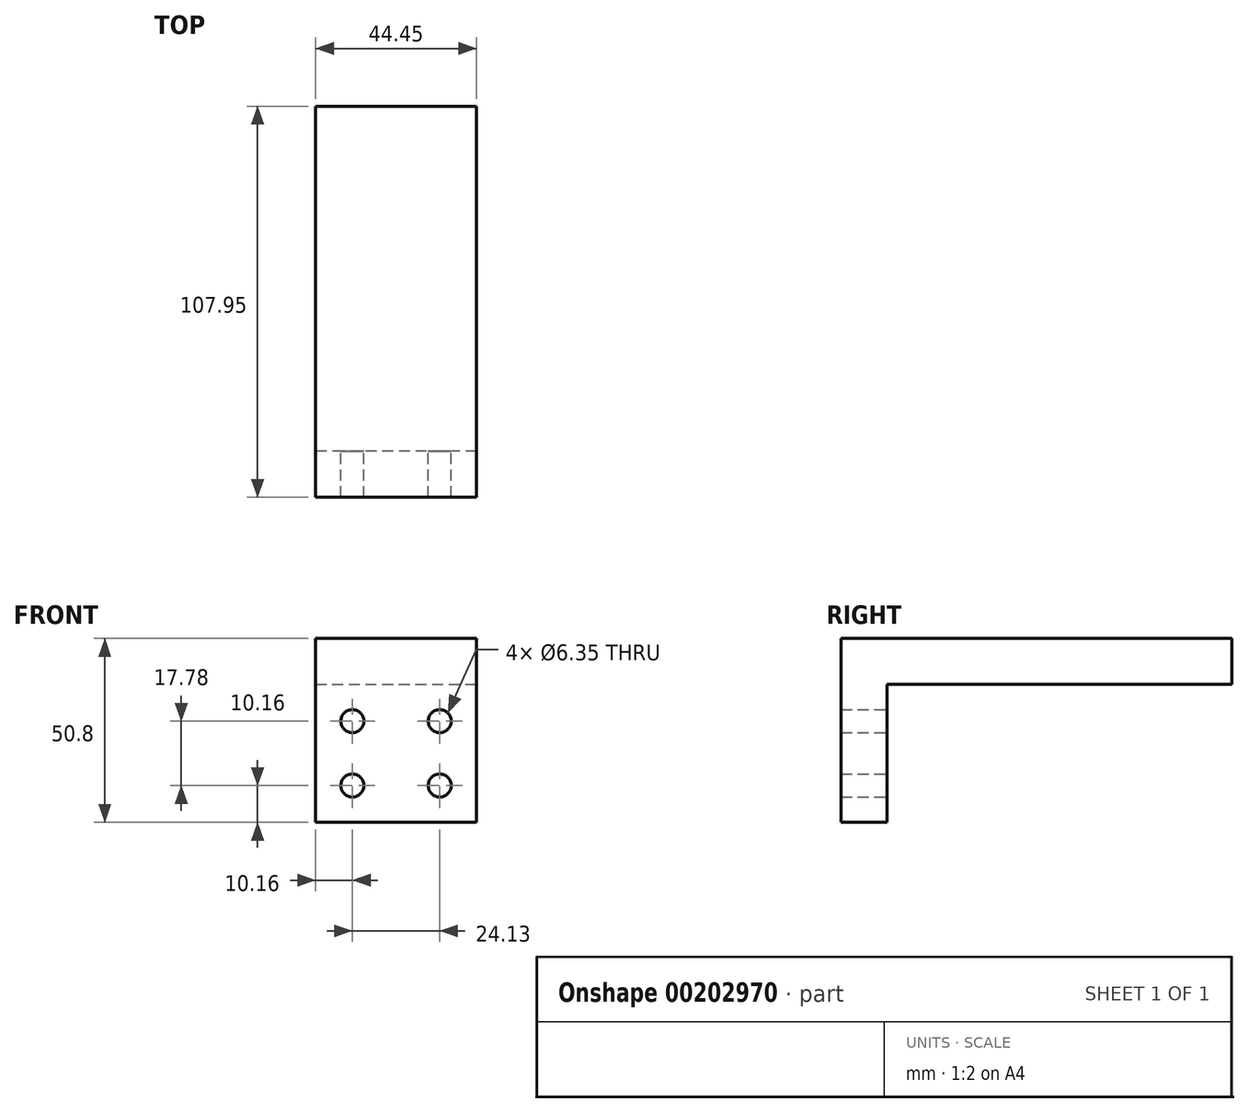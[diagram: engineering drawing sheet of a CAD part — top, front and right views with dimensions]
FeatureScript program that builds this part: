
annotation { "Feature Type Name" : "Feature", "Feature Type Description" : "" }
export const myFeature = defineFeature(function(context is Context, id is Id, definition is map)
    precondition{}
    {
        {
            var Q0;
            Q0=qCreatedBy(makeId("Top.planeOp"),FACE);
            var sketch = newSketch(context, id + "F0", { "sketchPlane" : qUnion([Q0])});
            skLineSegment(sketch, "E0.bottom", {"start": v(0, 0) * mm, "end": v(44.45, 0) * mm});
            skLineSegment(sketch, "E0.top", {"start": v(0, 107.95) * mm, "end": v(44.45, 107.95) * mm});
            skLineSegment(sketch, "E0.left", {"start": v(0, 0) * mm, "end": v(0, 107.95) * mm});
            skLineSegment(sketch, "E0.right", {"start": v(44.45, 0) * mm, "end": v(44.45, 107.95) * mm});
            skSolve(sketch);
        }
        {
            var Q0;
            Q0 = qSketchRegion(id + "F0", true);
            extrude(context, id + "F1", {"entities" : qUnion([Q0]), "depth" : 12.7 * mm});
        }
        {
            var Q0;
            Q0=makeQuery(id+"F1.opExtrude","CAP_FACE",FACE,{"disambiguationData":[OSD([sQuery(id+"F0.wireOp",EDGE,"E0.bottom"),sQuery(id+"F0.wireOp",EDGE,"E0.top"),sQuery(id+"F0.wireOp",EDGE,"E0.left"),sQuery(id+"F0.wireOp",EDGE,"E0.right")])],"isStart":true});
            var sketch = newSketch(context, id + "F2", { "sketchPlane" : qUnion([Q0])});
            skLineSegment(sketch, "E1.bottom", {"start": v(44.45, 0) * mm, "end": v(0, 0) * mm});
            skLineSegment(sketch, "E1.top", {"start": v(44.45, -12.7) * mm, "end": v(0, -12.7) * mm});
            skLineSegment(sketch, "E1.left", {"start": v(44.45, 0) * mm, "end": v(44.45, -12.7) * mm});
            skLineSegment(sketch, "E1.right", {"start": v(0, 0) * mm, "end": v(0, -12.7) * mm});
            skSolve(sketch);
        }
        {
            var Q0;
            Q0 = qSketchRegion(id + "F2", true);
            extrude(context, id + "F3", {"entities" : qUnion([Q0]), "operationType" : NewBodyOperationType.ADD, "depth" : 38.1 * mm});
        }
        {
            var Q0;
            Q0=makeQuery(id+"F3.opExtrude","SWEPT_FACE",FACE,{"disambiguationData":[OSD([sQuery(id+"F2.wireOp",EDGE,"E1.top")])]});
            var sketch = newSketch(context, id + "F4", { "sketchPlane" : qUnion([Q0])});
            skLineSegment(sketch, "E2.bottom", {"start": v(-44.45, 0) * mm, "end": v(-34.29, 0) * mm});
            skLineSegment(sketch, "E2.left", {"start": v(-44.45, 0) * mm, "end": v(-44.45, -10.16) * mm});
            skCircle(sketch, "E3", {"center": v(-34.29, -10.16) * mm, "radius": 3.18 * mm});
            skLineSegment(sketch, "E4", {"start": v(-44.45, -19.05) * mm, "end": v(0, -19.05) * mm});
            skLineSegment(sketch, "E5", {"start": v(-22.22, 0) * mm, "end": v(-22.22, -38.1) * mm});
            skCircle(sketch, "E6.MirrorC", {"center": v(-34.29, -27.94) * mm, "radius": 3.18 * mm});
            skCircle(sketch, "E7.MirrorC", {"center": v(-10.16, -10.16) * mm, "radius": 3.18 * mm});
            skCircle(sketch, "E8.MirrorC", {"center": v(-10.16, -27.94) * mm, "radius": 3.18 * mm});
            skSolve(sketch);
        }
        {
            var Q0;
            Q0 = qSketchRegion(id + "F4", true);
            extrude(context, id + "F5", {"entities" : qUnion([Q0]), "operationType" : NewBodyOperationType.REMOVE, "endBound" : BoundingType.THROUGH_ALL, "oppositeDirection" : true, "depth" : 25.4 * mm});
        }
    });
